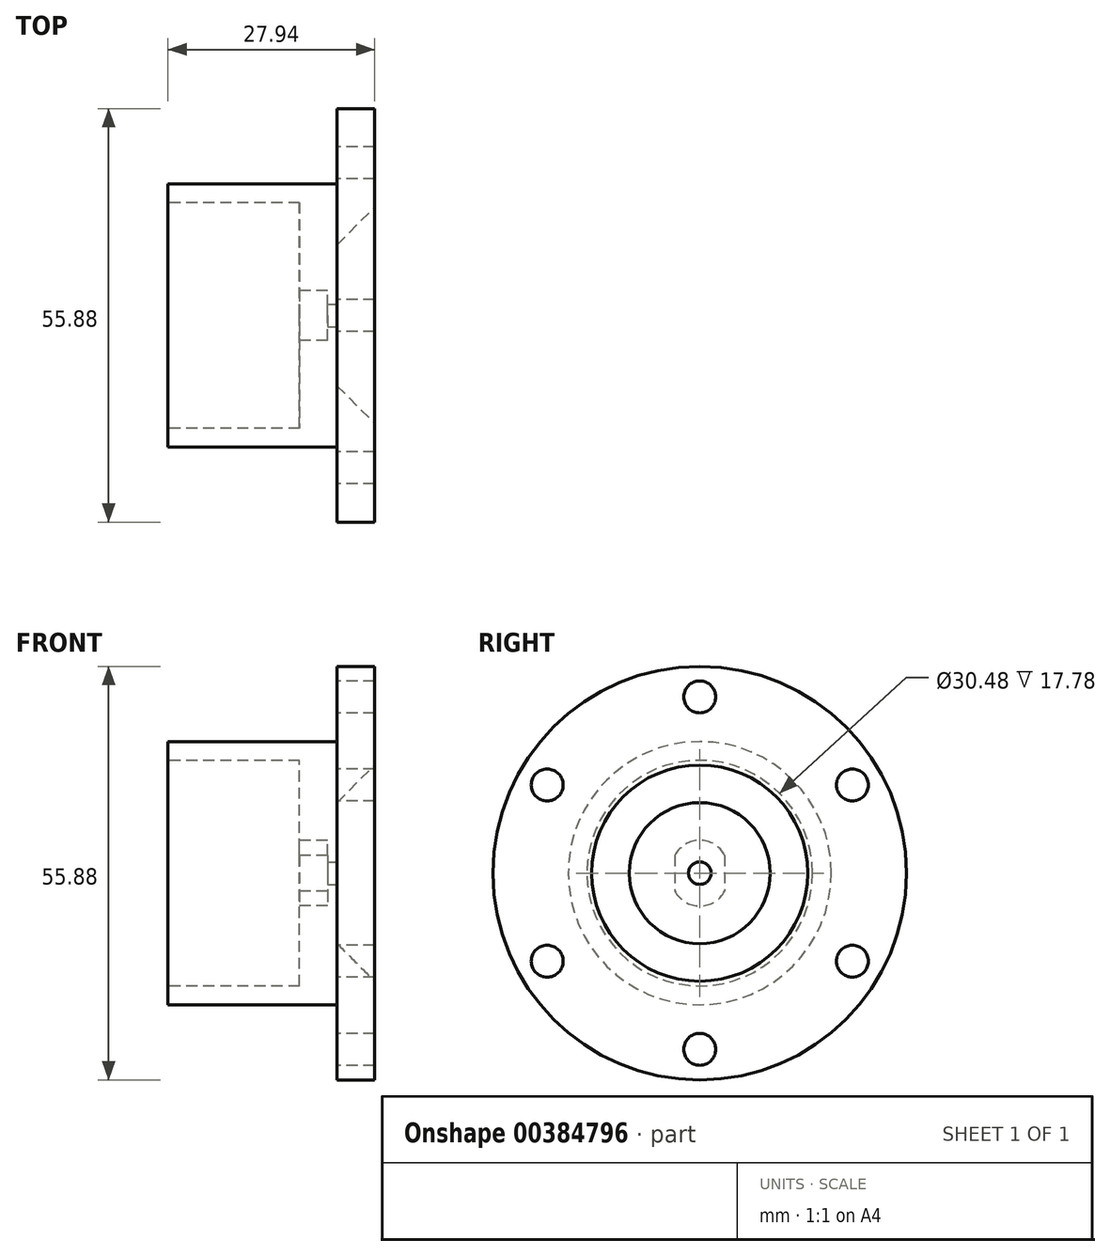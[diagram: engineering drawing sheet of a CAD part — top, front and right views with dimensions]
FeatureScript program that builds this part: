
annotation { "Feature Type Name" : "Feature", "Feature Type Description" : "" }
export const myFeature = defineFeature(function(context is Context, id is Id, definition is map)
    precondition{}
    {
        {
            var Q0;
            Q0=qCreatedBy(makeId("Right.planeOp"),FACE);
            var sketch = newSketch(context, id + "F0", { "sketchPlane" : qUnion([Q0])});
            skCircle(sketch, "E0", {"center": v(0, 0) * mm, "radius": 17.78 * mm});
            skCircle(sketch, "E1", {"center": v(0, 0) * mm, "radius": 15.24 * mm});
            skSolve(sketch);
        }
        {
            var Q0;
            Q0 = qSketchRegion(id + "F0", true);
            extrude(context, id + "F1", {"entities" : qUnion([Q0]), "depth" : 17.78 * mm});
        }
        {
            var Q0;
            Q0=makeQuery(id+"F1.opExtrude","CAP_FACE",FACE,{"disambiguationData":[OSD([sQuery(id+"F0.wireOp",EDGE,"E0"),sQuery(id+"F0.wireOp",EDGE,"E1")])],"isStart":false});
            var sketch = newSketch(context, id + "F2", { "sketchPlane" : qUnion([Q0])});
            skCircle(sketch, "E2.0", {"center": v(0, 0) * mm, "radius": 17.78 * mm});
            skSolve(sketch);
        }
        {
            var Q0;
            Q0 = qSketchRegion(id + "F2", true);
            extrude(context, id + "F3", {"entities" : qUnion([Q0]), "operationType" : NewBodyOperationType.ADD, "depth" : 5.08 * mm});
        }
        {
            var Q0;
            Q0=makeQuery(id+"F3.opExtrude","CAP_FACE",FACE,{"disambiguationData":[OSD([sQuery(id+"F2.wireOp",EDGE,"E2.0")])],"isStart":false});
            var sketch = newSketch(context, id + "F4", { "sketchPlane" : qUnion([Q0])});
            skCircle(sketch, "E3", {"center": v(0, 0) * mm, "radius": 1.52 * mm});
            skSolve(sketch);
        }
        {
            var Q0;
            Q0 = qSketchRegion(id + "F4", true);
            extrude(context, id + "F5", {"entities" : qUnion([Q0]), "operationType" : NewBodyOperationType.REMOVE, "oppositeDirection" : true, "depth" : 25.4 * mm});
        }
        {
            var Q0;
            Q0=makeQuery(id+"F3.opExtrude","CAP_FACE",FACE,{"disambiguationData":[OSD([sQuery(id+"F2.wireOp",EDGE,"E2.0")])],"isStart":false});
            var sketch = newSketch(context, id + "F6", { "sketchPlane" : qUnion([Q0])});
            skCircle(sketch, "E4", {"center": v(0, 0) * mm, "radius": 27.94 * mm});
            skCircle(sketch, "E5", {"center": v(0, 0) * mm, "radius": 9.53 * mm});
            skCircle(sketch, "E6", {"center": v(0, 23.81) * mm, "radius": 2.16 * mm});
            skCircle(sketch, "E7.1.0", {"center": v(-20.62, 11.9) * mm, "radius": 2.16 * mm});
            skCircle(sketch, "E7.2.0", {"center": v(-20.62, -11.9) * mm, "radius": 2.16 * mm});
            skCircle(sketch, "E7.3.0", {"center": v(0, -23.81) * mm, "radius": 2.16 * mm});
            skCircle(sketch, "E7.4.0", {"center": v(20.62, -11.9) * mm, "radius": 2.16 * mm});
            skCircle(sketch, "E7.5.0", {"center": v(20.62, 11.9) * mm, "radius": 2.16 * mm});
            skSolve(sketch);
        }
        {
            var Q0;
            Q0 = qSketchRegion(id + "F6", true);
            extrude(context, id + "F7", {"entities" : qUnion([Q0]), "operationType" : NewBodyOperationType.ADD, "depth" : 5.08 * mm});
        }
        {
            var Q0;
            Q0=makeQuery(id+"F7.opExtrude","CAP_EDGE",EDGE,{"disambiguationData":[OSD([sQuery(id+"F6.wireOp",EDGE,"E5")])],"isStart":false});
            chamfer(context, id + "F8", {"entities" : qUnion([Q0]), "width" : 5.08 * mm, "tangentPropagation" : true});
        }
        {
            var Q0;
            Q0=makeQuery(id+"F3.opExtrude","CAP_FACE",FACE,{"disambiguationData":[OSD([sQuery(id+"F2.wireOp",EDGE,"E2.0")])],"isStart":true});
            var sketch = newSketch(context, id + "F9", { "sketchPlane" : qUnion([Q0])});
            skLineSegment(sketch, "E8.left", {"start": v(-3.37, 2.41) * mm, "end": v(-3.37, -2.41) * mm});
            skLineSegment(sketch, "E8.right", {"start": v(3.37, 2.41) * mm, "end": v(3.37, -2.41) * mm});
            skPoint(sketch, "E8.middle", {"position": v(0, 0) * mm});
            skArc(sketch, "E9", {"start": v(3.37, 2.41) * mm, "mid": v(0, 4.44) * mm, "end": v(-3.37, 2.41) * mm});
            skPoint(sketch, "E10.orphan", {"position": v(-3.37, 4.38) * mm});
            skPoint(sketch, "E11.orphan", {"position": v(3.37, 4.38) * mm});
            skArc(sketch, "E12.MirrorCS", {"start": v(3.37, -2.41) * mm, "mid": v(0, -4.44) * mm, "end": v(-3.37, -2.41) * mm});
            skPoint(sketch, "E13.orphan", {"position": v(-3.37, -4.38) * mm});
            skPoint(sketch, "E14.orphan", {"position": v(3.37, -4.38) * mm});
            skSolve(sketch);
        }
        {
            var Q0;
            Q0 = qSketchRegion(id + "F9", true);
            extrude(context, id + "F10", {"entities" : qUnion([Q0]), "operationType" : NewBodyOperationType.REMOVE, "oppositeDirection" : true, "depth" : 3.8 * mm});
        }
    });
